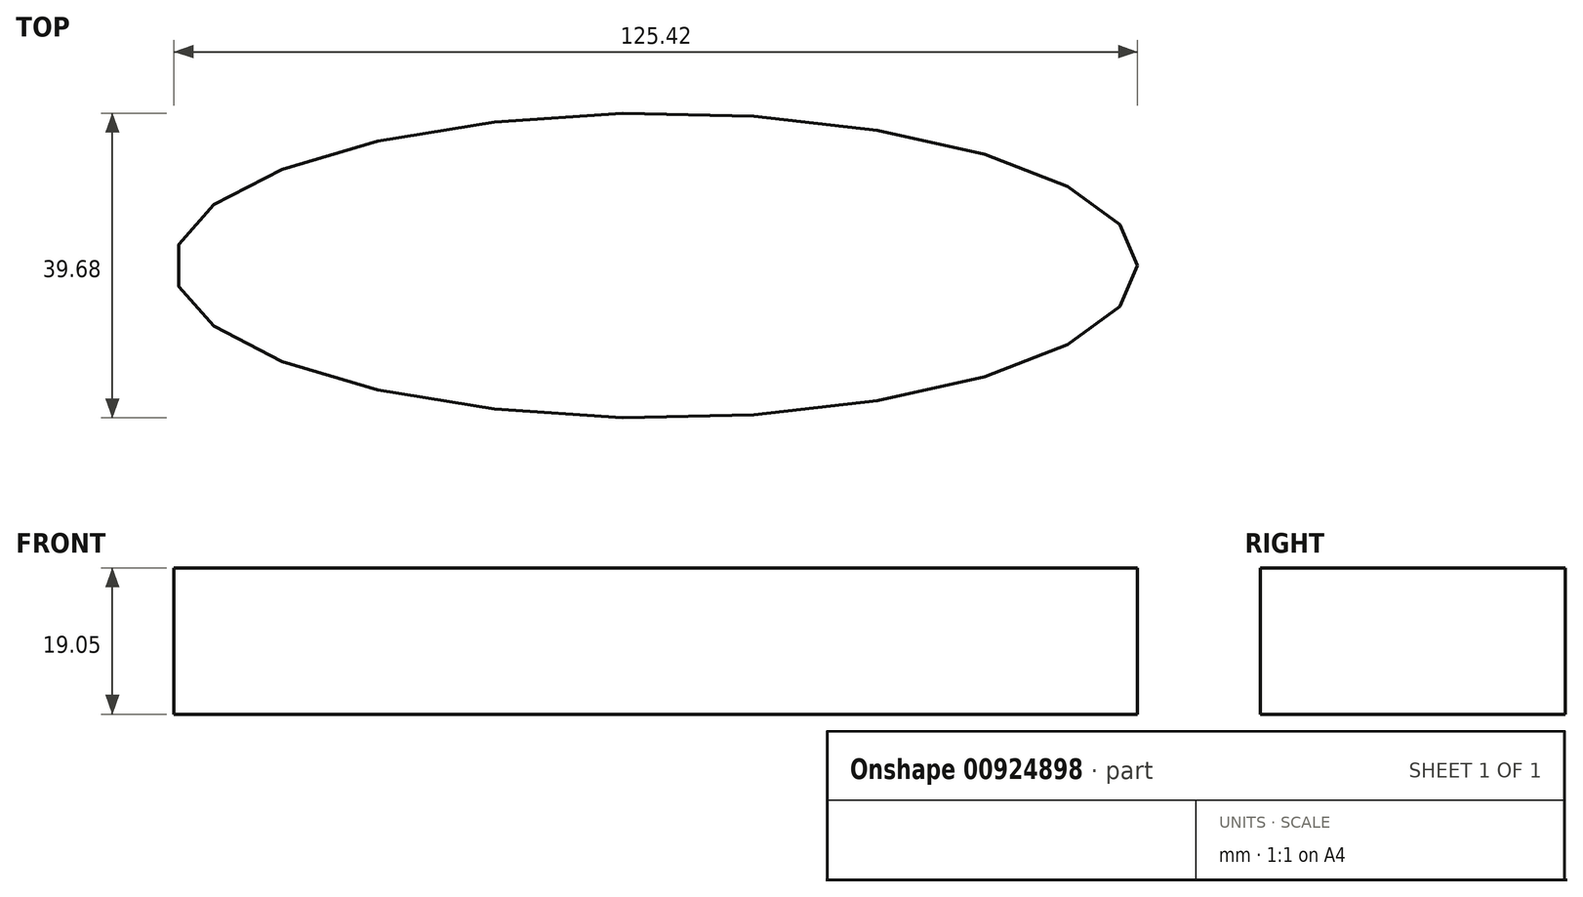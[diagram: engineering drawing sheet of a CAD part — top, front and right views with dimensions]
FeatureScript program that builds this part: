
annotation { "Feature Type Name" : "Feature", "Feature Type Description" : "" }
export const myFeature = defineFeature(function(context is Context, id is Id, definition is map)
    precondition{}
    {
        {
            var Q0;
            Q0=qCreatedBy(makeId("Top.planeOp"),FACE);
            var sketch = newSketch(context, id + "F0", { "sketchPlane" : qUnion([Q0])});
            skEllipse(sketch, "E0", {"center": v(0, 0) * mm, "majorRadius": 62.7 * mm, "minorRadius": 19.84 * mm, "majorAxis": v(1, 0)});
            skEllipse(sketch, "E1", {"center": v(0, 0) * mm, "majorRadius": 61.12 * mm, "minorRadius": 18.97 * mm, "majorAxis": v(1, 0)});
            skSolve(sketch);
        }
        {
            var Q0;
            Q0 = qSketchRegion(id + "F0", true);
            var Q1;
            Q1=makeQuery(id+"F0.imprint","IMPRINT",FACE,{"disambiguationData":[TD([[makeQuery(id+"F0.imprint","IMPRINT",EDGE,{"derivedFrom":sQuery(id+"F0.wireOp",EDGE,"E1")}),1.0]])]});
            extrude(context, id + "F1", {"entities" : qUnion([Q0, Q1]), "oppositeDirection" : true, "depth" : 19.05 * mm, "offsetDistance" : 25.4 * mm});
        }
    });
